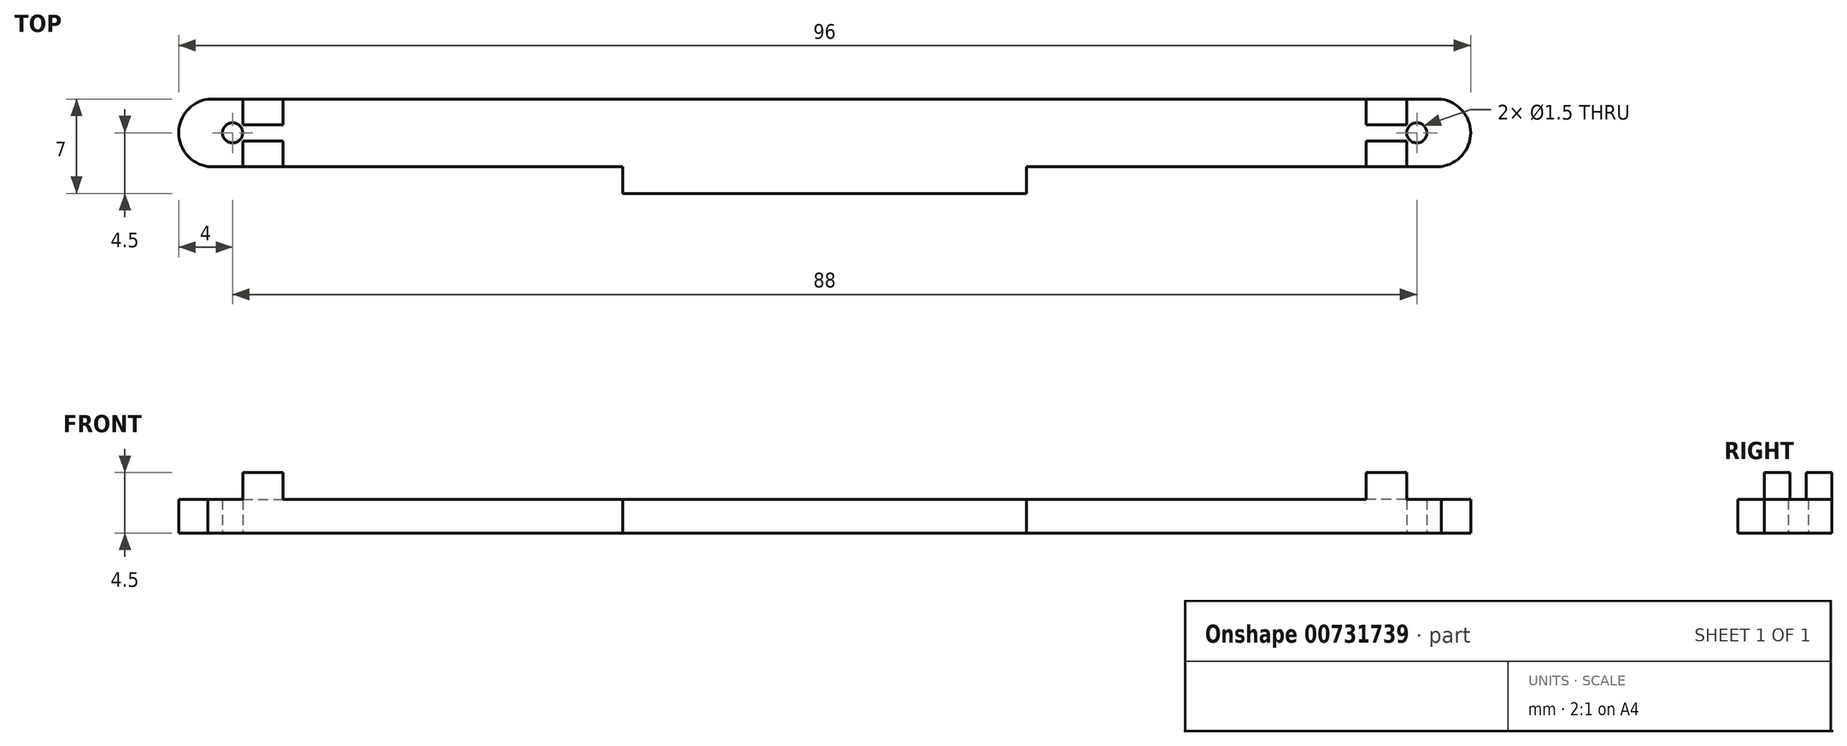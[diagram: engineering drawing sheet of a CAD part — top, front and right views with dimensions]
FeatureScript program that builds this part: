
annotation { "Feature Type Name" : "Feature", "Feature Type Description" : "" }
export const myFeature = defineFeature(function(context is Context, id is Id, definition is map)
    precondition{}
    {
        {
            var Q0;
            Q0=qCreatedBy(makeId("Top.planeOp"),FACE);
            var sketch = newSketch(context, id + "F0", { "sketchPlane" : qUnion([Q0])});
            skLineSegment(sketch, "E0", {"start": v(-44, 0) * mm, "end": v(44, 0) * mm, "construction": true});
            skPoint(sketch, "E1", {"position": v(0, 0) * mm});
            skCircle(sketch, "E2", {"center": v(-44, 0) * mm, "radius": 0.75 * mm});
            skCircle(sketch, "E3.MirrorC", {"center": v(44, 0) * mm, "radius": 0.75 * mm});
            skLineSegment(sketch, "E4", {"start": v(-45.83, 2.5) * mm, "end": v(45.83, 2.5) * mm});
            skPoint(sketch, "E5", {"position": v(0, 2.5) * mm});
            skLineSegment(sketch, "E6", {"start": v(-15, -4.5) * mm, "end": v(15, -4.5) * mm});
            skLineSegment(sketch, "E7.MirrorCS", {"start": v(-45.83, -2.5) * mm, "end": v(-15, -2.5) * mm});
            skPoint(sketch, "E8", {"position": v(0, -4.5) * mm});
            skLineSegment(sketch, "E9", {"start": v(-15, -4.5) * mm, "end": v(-15, -2.5) * mm});
            skLineSegment(sketch, "E10", {"start": v(15, -4.5) * mm, "end": v(15, -2.5) * mm});
            skLineSegment(sketch, "E11.trimOffspring", {"start": v(15, -2.5) * mm, "end": v(45.83, -2.5) * mm});
            skArc(sketch, "E12", {"start": v(-45.83, 2.5) * mm, "mid": v(-48, 0) * mm, "end": v(-45.83, -2.5) * mm});
            skPoint(sketch, "E13", {"position": v(-48, 0) * mm});
            skPoint(sketch, "E14.orphan", {"position": v(-48, 2.5) * mm});
            skPoint(sketch, "E15.orphan", {"position": v(-48, -2.5) * mm});
            skArc(sketch, "E16.MirrorCS", {"start": v(45.83, 2.5) * mm, "mid": v(48, 0) * mm, "end": v(45.83, -2.5) * mm});
            skPoint(sketch, "E17.orphan", {"position": v(48, 2.5) * mm});
            skPoint(sketch, "E18.orphan", {"position": v(48, -2.5) * mm});
            skSolve(sketch);
        }
        {
            var Q0;
            Q0=makeQuery(id+"F0.imprint","IMPRINT",FACE,{"disambiguationData":[TD([[makeQuery(id+"F0.imprint","IMPRINT",EDGE,{"derivedFrom":sQuery(id+"F0.wireOp",EDGE,"E2")}),-1.0]])]});
            extrude(context, id + "F1", {"entities" : qUnion([Q0]), "depth" : 2.5 * mm, "offsetDistance" : 25 * mm});
        }
        {
            var Q0;
            Q0=makeQuery(id+"F1.opExtrude","CAP_FACE",FACE,{"disambiguationData":[OSD([sQuery(id+"F0.wireOp",EDGE,"E2"),sQuery(id+"F0.wireOp",EDGE,"E3.MirrorC"),sQuery(id+"F0.wireOp",EDGE,"E4"),sQuery(id+"F0.wireOp",EDGE,"E6"),sQuery(id+"F0.wireOp",EDGE,"E7.MirrorCS"),sQuery(id+"F0.wireOp",EDGE,"E9"),sQuery(id+"F0.wireOp",EDGE,"E10"),sQuery(id+"F0.wireOp",EDGE,"E11.trimOffspring"),sQuery(id+"F0.wireOp",EDGE,"E12"),sQuery(id+"F0.wireOp",EDGE,"E16.MirrorCS")])],"isStart":false});
            var sketch = newSketch(context, id + "F2", { "sketchPlane" : qUnion([Q0])});
            skPoint(sketch, "E19", {"position": v(-43.25, 0) * mm});
            skLineSegment(sketch, "E20.bottom", {"start": v(-43.25, 2.5) * mm, "end": v(-40.25, 2.5) * mm});
            skLineSegment(sketch, "E20.top", {"start": v(-43.25, 0.6) * mm, "end": v(-40.25, 0.6) * mm});
            skLineSegment(sketch, "E20.left", {"start": v(-43.25, 2.5) * mm, "end": v(-43.25, 0.6) * mm});
            skLineSegment(sketch, "E20.right", {"start": v(-40.25, 2.5) * mm, "end": v(-40.25, 0.6) * mm});
            skLineSegment(sketch, "E21.MirrorCS", {"start": v(-40.25, -2.5) * mm, "end": v(-40.25, -0.6) * mm});
            skLineSegment(sketch, "E22.MirrorCS", {"start": v(-43.25, -0.6) * mm, "end": v(-40.25, -0.6) * mm});
            skLineSegment(sketch, "E23.MirrorCS", {"start": v(-43.25, -2.5) * mm, "end": v(-43.25, -0.6) * mm});
            skLineSegment(sketch, "E24.MirrorCS", {"start": v(43.25, -0.6) * mm, "end": v(40.25, -0.6) * mm});
            skLineSegment(sketch, "E25.MirrorCS", {"start": v(43.25, -2.5) * mm, "end": v(43.25, -0.6) * mm});
            skLineSegment(sketch, "E26.MirrorCS", {"start": v(40.25, -2.5) * mm, "end": v(40.25, -0.6) * mm});
            skLineSegment(sketch, "E27.MirrorCS", {"start": v(40.25, 2.5) * mm, "end": v(40.25, 0.6) * mm});
            skLineSegment(sketch, "E28.MirrorCS", {"start": v(43.25, 0.6) * mm, "end": v(40.25, 0.6) * mm});
            skLineSegment(sketch, "E29.MirrorCS", {"start": v(43.25, 2.5) * mm, "end": v(43.25, 0.6) * mm});
            skSolve(sketch);
        }
        {
            var Q0;
            Q0=makeQuery(id+"F2.imprint","IMPRINT",FACE,{"disambiguationData":[TD([[makeQuery(id+"F2.imprint","IMPRINT",EDGE,{"derivedFrom":sQuery(id+"F2.wireOp",EDGE,"E20.bottom")}),-1.0]])]});
            var Q1;
            {var subQ0=sQuery(id+"F2.wireOp",EDGE,"E21.MirrorCS");Q1=makeQuery(id+"F2.imprint","IMPRINT",FACE,{"disambiguationData":[TD([[makeQuery(id+"F2.imprint","IMPRINT",EDGE,{"derivedFrom":subQ0}),1.0]])]});}
            var Q2;
            Q2=makeQuery(id+"F2.imprint","IMPRINT",FACE,{"disambiguationData":[TD([[makeQuery(id+"F2.imprint","IMPRINT",EDGE,{"derivedFrom":sQuery(id+"F2.wireOp",EDGE,"E24.MirrorCS")}),1.0]])]});
            var Q3;
            {var subQ0=sQuery(id+"F2.wireOp",EDGE,"E27.MirrorCS");Q3=makeQuery(id+"F2.imprint","IMPRINT",FACE,{"disambiguationData":[TD([[makeQuery(id+"F2.imprint","IMPRINT",EDGE,{"derivedFrom":subQ0}),1.0]])]});}
            extrude(context, id + "F3", {"entities" : qUnion([Q0, Q1, Q2, Q3]), "operationType" : NewBodyOperationType.ADD, "depth" : 2 * mm, "offsetDistance" : 25 * mm});
        }
    });
